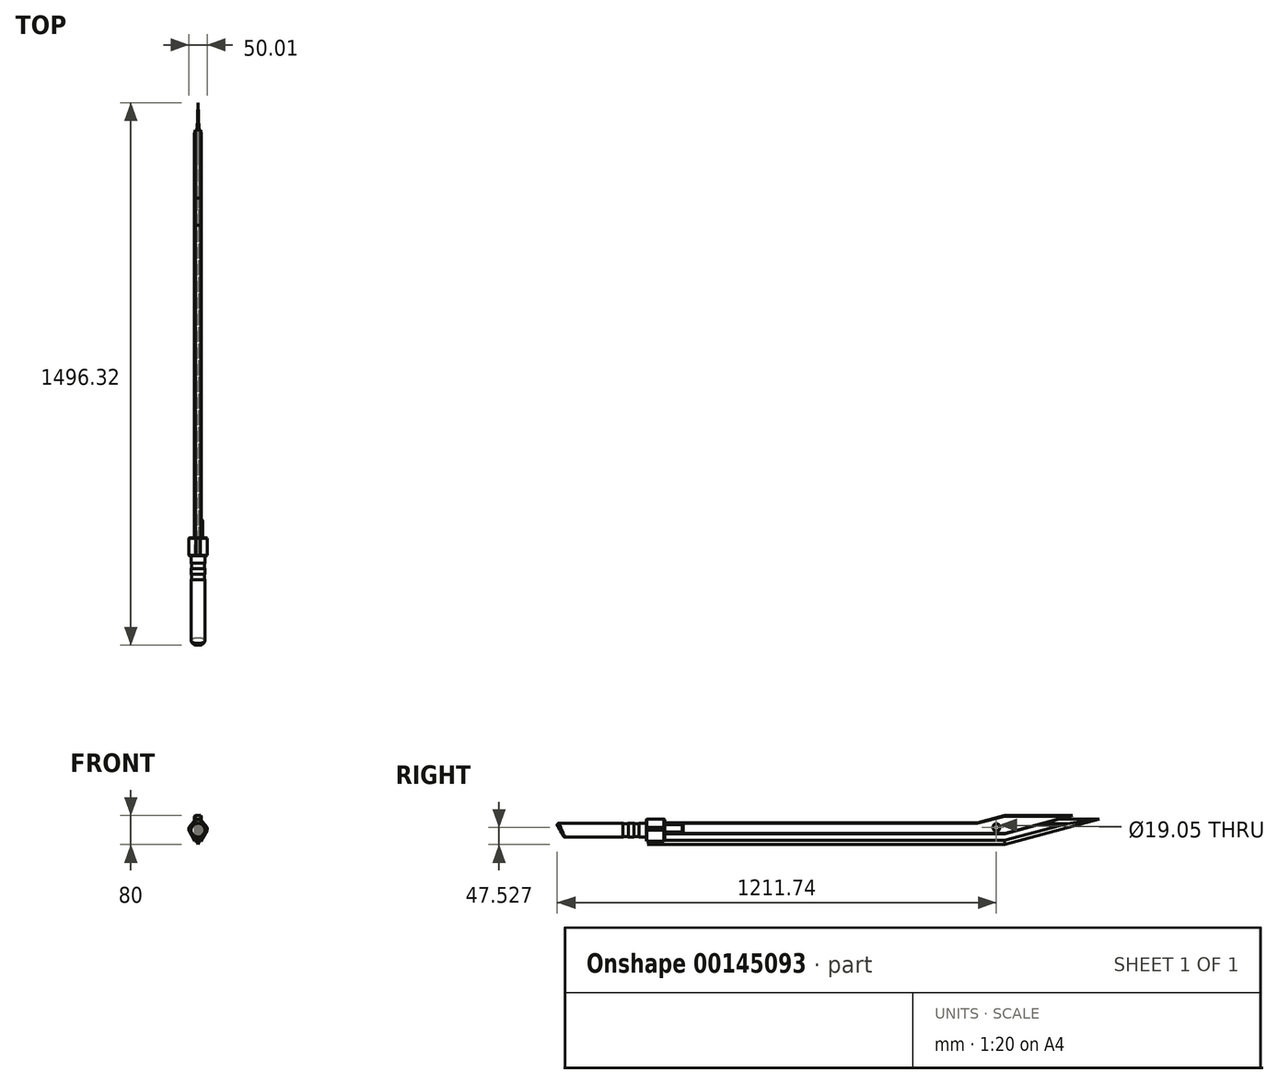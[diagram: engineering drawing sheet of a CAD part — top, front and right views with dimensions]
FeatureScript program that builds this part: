
annotation { "Feature Type Name" : "Feature", "Feature Type Description" : "" }
export const myFeature = defineFeature(function(context is Context, id is Id, definition is map)
    precondition{}
    {
        {
            var Q0;
            Q0=qCreatedBy(makeId("Right.planeOp"),FACE);
            var sketch = newSketch(context, id + "F0", { "sketchPlane" : qUnion([Q0])});
            skLineSegment(sketch, "E0", {"start": v(0, 0) * mm, "end": v(0, -19.92) * mm});
            skLineSegment(sketch, "E1", {"start": v(0, -19.92) * mm, "end": v(-47.25, -50) * mm});
            skLineSegment(sketch, "E2", {"start": v(-47.25, -50) * mm, "end": v(938.76, -50) * mm});
            skLineSegment(sketch, "E3", {"start": v(0, 0) * mm, "end": v(864.12, 0) * mm});
            skLineSegment(sketch, "E4", {"start": v(864.12, 0) * mm, "end": v(938.76, 20) * mm});
            skLineSegment(sketch, "E5", {"start": v(938.76, 20) * mm, "end": v(1200, 20) * mm});
            skLineSegment(sketch, "E6", {"start": v(1200, 20) * mm, "end": v(938.76, -50) * mm});
            skSolve(sketch);
        }
        {
            var Q0;
            Q0=makeQuery(id+"F0.imprint","IMPRINT",FACE,{"disambiguationData":[TD([[makeQuery(id+"F0.imprint","IMPRINT",EDGE,{"derivedFrom":sQuery(id+"F0.wireOp",EDGE,"E0")}),1.0]])]});
            extrude(context, id + "F1", {"entities" : qUnion([Q0]), "depth" : 6.35 * mm});
        }
        {
            var Q0;
            Q0=makeQuery(id+"F1.opExtrude","CAP_FACE",FACE,{"disambiguationData":[OSD([sQuery(id+"F0.wireOp",EDGE,"E0"),sQuery(id+"F0.wireOp",EDGE,"E1"),sQuery(id+"F0.wireOp",EDGE,"E2"),sQuery(id+"F0.wireOp",EDGE,"E3"),sQuery(id+"F0.wireOp",EDGE,"E4"),sQuery(id+"F0.wireOp",EDGE,"E5"),sQuery(id+"F0.wireOp",EDGE,"E6")])],"isStart":false});
            var sketch = newSketch(context, id + "F2", { "sketchPlane" : qUnion([Q0])});
            skLineSegment(sketch, "E7", {"start": v(0, -20) * mm, "end": v(938.76, -20) * mm});
            skPoint(sketch, "E8", {"position": v(1069.38, 20) * mm});
            skLineSegment(sketch, "E9", {"start": v(937.44, 30) * mm, "end": v(862.8, 10) * mm});
            skLineSegment(sketch, "E10", {"start": v(862.8, 10) * mm, "end": v(0, 10) * mm});
            skLineSegment(sketch, "E11", {"start": v(0, 10) * mm, "end": v(0, -20) * mm});
            skLineSegment(sketch, "E12", {"start": v(937.44, 30) * mm, "end": v(1125.36, 30) * mm});
            skLineSegment(sketch, "E13", {"start": v(1125.36, 30) * mm, "end": v(938.76, -20) * mm});
            skSolve(sketch);
        }
        {
            var Q0;
            Q0 = qSketchRegion(id + "F2", true);
            extrude(context, id + "F3", {"entities" : qUnion([Q0]), "operationType" : NewBodyOperationType.ADD, "depth" : 6.35 * mm});
        }
        {
            var Q0;
            Q0=makeQuery(id+"F3.opExtrude","CAP_FACE",FACE,{"disambiguationData":[OSD([sQuery(id+"F2.wireOp",EDGE,"E7"),sQuery(id+"F2.wireOp",EDGE,"E9"),sQuery(id+"F2.wireOp",EDGE,"E10"),sQuery(id+"F2.wireOp",EDGE,"E11"),sQuery(id+"F2.wireOp",EDGE,"E12"),sQuery(id+"F2.wireOp",EDGE,"E13")])],"isStart":true});
            var sketch = newSketch(context, id + "F4", { "sketchPlane" : qUnion([Q0])});
            skLineSegment(sketch, "E14", {"start": v(-1125.36, 30) * mm, "end": v(-1088.04, 20) * mm});
            skLineSegment(sketch, "E15", {"start": v(-1088.04, 20) * mm, "end": v(-938.76, 20) * mm});
            skLineSegment(sketch, "E16", {"start": v(-938.76, 20) * mm, "end": v(-864.12, 0) * mm});
            skLineSegment(sketch, "E17", {"start": v(-864.12, 0) * mm, "end": v(0, 0) * mm});
            skLineSegment(sketch, "E18", {"start": v(0, 0) * mm, "end": v(0, 10) * mm});
            skLineSegment(sketch, "E19", {"start": v(0, 10) * mm, "end": v(-862.8, 10) * mm});
            skLineSegment(sketch, "E20", {"start": v(-862.8, 10) * mm, "end": v(-937.44, 30) * mm});
            skLineSegment(sketch, "E21", {"start": v(-937.44, 30) * mm, "end": v(-1125.36, 30) * mm});
            skSolve(sketch);
        }
        {
            var Q0;
            Q0 = qSketchRegion(id + "F4", true);
            extrude(context, id + "F5", {"entities" : qUnion([Q0]), "operationType" : NewBodyOperationType.ADD, "depth" : 6.35 * mm});
        }
        {
            var Q0;
            Q0=makeQuery(id+"F5.boolean.opBoolean","MERGE",FACE,{"derivedFrom":[makeQuery(id+"F1.opExtrude","CAP_FACE",FACE,{"disambiguationData":[OSD([sQuery(id+"F0.wireOp",EDGE,"E0"),sQuery(id+"F0.wireOp",EDGE,"E1"),sQuery(id+"F0.wireOp",EDGE,"E2"),sQuery(id+"F0.wireOp",EDGE,"E3"),sQuery(id+"F0.wireOp",EDGE,"E4"),sQuery(id+"F0.wireOp",EDGE,"E5"),sQuery(id+"F0.wireOp",EDGE,"E6")])],"isStart":true}),makeQuery(id+"F5.opExtrude","CAP_FACE",FACE,{"disambiguationData":[OSD([sQuery(id+"F4.wireOp",EDGE,"E14"),sQuery(id+"F4.wireOp",EDGE,"E15"),sQuery(id+"F4.wireOp",EDGE,"E16"),sQuery(id+"F4.wireOp",EDGE,"E17"),sQuery(id+"F4.wireOp",EDGE,"E18"),sQuery(id+"F4.wireOp",EDGE,"E19"),sQuery(id+"F4.wireOp",EDGE,"E20"),sQuery(id+"F4.wireOp",EDGE,"E21")])],"isStart":false})]});
            var sketch = newSketch(context, id + "F6", { "sketchPlane" : qUnion([Q0])});
            skLineSegment(sketch, "E22", {"start": v(0, 10) * mm, "end": v(0, -20) * mm});
            skLineSegment(sketch, "E23", {"start": v(0, -20) * mm, "end": v(-938.76, -20) * mm});
            skLineSegment(sketch, "E24", {"start": v(-938.76, -20) * mm, "end": v(-1125.36, 30) * mm});
            skLineSegment(sketch, "E25", {"start": v(-1125.36, 30) * mm, "end": v(-937.44, 30) * mm});
            skLineSegment(sketch, "E26", {"start": v(-937.44, 30) * mm, "end": v(-862.8, 10) * mm});
            skLineSegment(sketch, "E27", {"start": v(-862.8, 10) * mm, "end": v(0, 10) * mm});
            skSolve(sketch);
        }
        {
            var Q0;
            Q0 = qSketchRegion(id + "F6", true);
            extrude(context, id + "F7", {"entities" : qUnion([Q0]), "operationType" : NewBodyOperationType.ADD, "depth" : 6.35 * mm});
        }
        {
            var Q0;
            Q0=makeQuery(id+"F7.boolean.opBoolean","MERGE",FACE,{"derivedFrom":[makeQuery(id+"F5.boolean.opBoolean","MERGE",FACE,{"derivedFrom":[makeQuery(id+"F3.boolean.opBoolean","MERGE",FACE,{"derivedFrom":[makeQuery(id+"F1.opExtrude","SWEPT_FACE",FACE,{"disambiguationData":[OSD([sQuery(id+"F0.wireOp",EDGE,"E0")])]}),makeQuery(id+"F3.opExtrude","SWEPT_FACE",FACE,{"disambiguationData":[OSD([sQuery(id+"F2.wireOp",EDGE,"E11")])]})]}),makeQuery(id+"F5.opExtrude","SWEPT_FACE",FACE,{"disambiguationData":[OSD([sQuery(id+"F4.wireOp",EDGE,"E18")])]})]}),makeQuery(id+"F7.opExtrude","SWEPT_FACE",FACE,{"disambiguationData":[OSD([sQuery(id+"F6.wireOp",EDGE,"E22")])]})]});
            var sketch = newSketch(context, id + "F8", { "sketchPlane" : qUnion([Q0])});
            skLineSegment(sketch, "E28.top", {"start": v(-21.82, -40) * mm, "end": v(28.18, -40) * mm});
            skLineSegment(sketch, "E28.left", {"start": v(-21.82, 20) * mm, "end": v(-21.82, -40) * mm});
            skLineSegment(sketch, "E28.right", {"start": v(28.18, 20) * mm, "end": v(28.18, -40) * mm});
            skLineSegment(sketch, "E29", {"start": v(-21.82, 20) * mm, "end": v(28.18, 20) * mm});
            skSolve(sketch);
        }
        {
            var Q0;
            Q0 = qSketchRegion(id + "F8", true);
            extrude(context, id + "F9", {"entities" : qUnion([Q0]), "operationType" : NewBodyOperationType.ADD, "depth" : 50 * mm});
        }
        {
            var Q0;
            Q0=makeQuery(id+"F9.opExtrude","CAP_FACE",FACE,{"disambiguationData":[OSD([sQuery(id+"F8.wireOp",EDGE,"E28.bottom"),sQuery(id+"F8.wireOp",EDGE,"E28.top"),sQuery(id+"F8.wireOp",EDGE,"E28.left"),sQuery(id+"F8.wireOp",EDGE,"E28.right")])],"isStart":false});
            var sketch = newSketch(context, id + "F10", { "sketchPlane" : qUnion([Q0])});
            skPoint(sketch, "E30.centerSnap0", {"position": v(3.18, -40) * mm});
            skCircle(sketch, "E31", {"center": v(3.17, -10) * mm, "radius": 19.05 * mm});
            skSolve(sketch);
        }
        {
            var Q0;
            Q0 = qSketchRegion(id + "F10", true);
            extrude(context, id + "F11", {"entities" : qUnion([Q0]), "operationType" : NewBodyOperationType.ADD, "depth" : 250 * mm});
        }
        {
            var Q0;
            Q0=makeQuery(id+"F1.opExtrude","CAP_EDGE",EDGE,{"disambiguationData":[OSD([sQuery(id+"F0.wireOp",EDGE,"E2")])],"isStart":false});
            var Q1;
            Q1=makeQuery(id+"F1.opExtrude","CAP_EDGE",EDGE,{"disambiguationData":[OSD([sQuery(id+"F0.wireOp",EDGE,"E2")])],"isStart":true});
            var Q2;
            Q2=makeQuery(id+"F1.opExtrude","CAP_EDGE",EDGE,{"disambiguationData":[OSD([sQuery(id+"F0.wireOp",EDGE,"E6")])],"isStart":false});
            var Q3;
            {var subQ1=sQuery(id+"F0.wireOp",EDGE,"E5");var subQ2=sQuery(id+"F0.wireOp",EDGE,"E6");Q3=makeQuery(id+"F3.boolean.opBoolean","SPLIT",EDGE,{"disambiguationData":[TD([makeQuery(id+"F1.opExtrude","SWEPT_FACE",FACE,{"disambiguationData":[OSD([subQ2])]})])],"derivedFrom":makeQuery(id+"F1.opExtrude","CAP_EDGE",EDGE,{"disambiguationData":[OSD([subQ1])],"isStart":false})});}
            var Q4;
            Q4=makeQuery(id+"F1.opExtrude","CAP_EDGE",EDGE,{"disambiguationData":[OSD([sQuery(id+"F0.wireOp",EDGE,"E5")])],"isStart":true});
            var Q5;
            Q5=makeQuery(id+"F1.opExtrude","CAP_EDGE",EDGE,{"disambiguationData":[OSD([sQuery(id+"F0.wireOp",EDGE,"E6")])],"isStart":true});
            chamfer(context, id + "F12", {"entities" : qUnion([Q0, Q1, Q2, Q3, Q4, Q5]), "chamferType" : ChamferType.OFFSET_ANGLE, "width" : 3.17 * mm, "oppositeDirection" : true, "angle" : 75 * degree, "tangentPropagation" : true});
        }
        {
            var Q0;
            Q0=qCreatedBy(makeId("Right.planeOp"),FACE);
            cPlane(context, id + "F13", {"entities" : qUnion([Q0]), "cplaneType" : CPlaneType.OFFSET, "offset" : 3.17 * mm, "width" : 150 * mm, "height" : 150 * mm});
        }
        {
            var Q0;
            Q0=qCreatedBy(id+"F13.planeOp",FACE);
            var sketch = newSketch(context, id + "F14", { "sketchPlane" : qUnion([Q0])});
            skLineSegment(sketch, "E32.bottom", {"start": v(-115, 9.05) * mm, "end": v(-100, 9.05) * mm});
            skLineSegment(sketch, "E32.top", {"start": v(-115, 7.8) * mm, "end": v(-100, 7.8) * mm});
            skLineSegment(sketch, "E32.left", {"start": v(-115, 9.05) * mm, "end": v(-115, 7.8) * mm});
            skLineSegment(sketch, "E32.right", {"start": v(-100, 9.05) * mm, "end": v(-100, 7.8) * mm});
            skLineSegment(sketch, "E33.bottom", {"start": v(-85, 9.05) * mm, "end": v(-70, 9.05) * mm});
            skLineSegment(sketch, "E33.top", {"start": v(-85, 7.8) * mm, "end": v(-70, 7.8) * mm});
            skLineSegment(sketch, "E33.left", {"start": v(-85, 9.05) * mm, "end": v(-85, 7.8) * mm});
            skLineSegment(sketch, "E33.right", {"start": v(-70, 9.05) * mm, "end": v(-70, 7.8) * mm});
            skLineSegment(sketch, "E34", {"start": v(-220.02, -10) * mm, "end": v(-50, -10) * mm});
            skSolve(sketch);
        }
        {
            var Q0;
            Q0 = qSketchRegion(id + "F14", true);
            var Q1;
            Q1=sQuery(id+"F14.wireOp",EDGE,"E34");
            revolve(context, id + "F15", {"operationType" : NewBodyOperationType.REMOVE, "entities" : qUnion([Q0]), "axis" : qUnion([Q1]), "revolveType" : RevolveType.FULL, "oppositeDirection" : true});
        }
        {
            var Q0;
            Q0=makeQuery(id+"F15.boolean.opBoolean","COPY",FACE,{"derivedFrom":makeQuery(id+"F15.opRevolve","SWEPT_FACE",FACE,{"disambiguationData":[OSD([sQuery(id+"F14.wireOp",EDGE,"E32.top")])]})});
            var Q1;
            Q1=makeQuery(id+"F15.boolean.opBoolean","COPY",FACE,{"derivedFrom":makeQuery(id+"F15.opRevolve","SWEPT_FACE",FACE,{"disambiguationData":[OSD([sQuery(id+"F14.wireOp",EDGE,"E33.top")])]})});
            fillet(context, id + "F16", {"entities" : qUnion([Q0, Q1]), "radius" : 5 * mm, "tangentPropagation" : true, "allowEdgeOverflow" : false});
        }
        {
            var Q0;
            Q0=makeQuery(id+"F9.opExtrude","SWEPT_EDGE",EDGE,{"disambiguationData":[OSD([sQuery(id+"F8.wireOp",EDGE,"E28.right"),sQuery(id+"F8.wireOp",EDGE,"E29")])]});
            var Q1;
            Q1=makeQuery(id+"F9.opExtrude","SWEPT_EDGE",EDGE,{"disambiguationData":[OSD([sQuery(id+"F8.wireOp",EDGE,"E28.left"),sQuery(id+"F8.wireOp",EDGE,"E29")])]});
            chamfer(context, id + "F17", {"entities" : qUnion([Q0, Q1]), "chamferType" : ChamferType.OFFSET_ANGLE, "width" : 18.8 * mm, "oppositeDirection" : false, "angle" : 50 * degree, "tangentPropagation" : true});
        }
        {
            var Q0;
            Q0=makeQuery(id+"F9.opExtrude","SWEPT_EDGE",EDGE,{"disambiguationData":[OSD([sQuery(id+"F8.wireOp",EDGE,"E28.top"),sQuery(id+"F8.wireOp",EDGE,"E28.right")])]});
            var Q1;
            Q1=makeQuery(id+"F9.opExtrude","SWEPT_EDGE",EDGE,{"disambiguationData":[OSD([sQuery(id+"F8.wireOp",EDGE,"E28.top"),sQuery(id+"F8.wireOp",EDGE,"E28.left")])]});
            chamfer(context, id + "F18", {"entities" : qUnion([Q0, Q1]), "chamferType" : ChamferType.OFFSET_ANGLE, "width" : 30 * mm, "oppositeDirection" : false, "angle" : 29 * degree, "tangentPropagation" : true});
        }
        {
            var Q0;
            Q0=qCreatedBy(makeId("Right.planeOp"),FACE);
            var sketch = newSketch(context, id + "F19", { "sketchPlane" : qUnion([Q0])});
            skLineSegment(sketch, "E35", {"start": v(-300, 9.08) * mm, "end": v(-277.97, -29.08) * mm});
            skLineSegment(sketch, "E36", {"start": v(-300, -29.08) * mm, "end": v(-300, 9.08) * mm});
            skLineSegment(sketch, "E37", {"start": v(-300, -29.08) * mm, "end": v(-277.97, -29.08) * mm});
            skSolve(sketch);
        }
        {
            var Q0;
            Q0=makeQuery(id+"F19.imprint","IMPRINT",FACE,{"disambiguationData":[TD([[makeQuery(id+"F19.imprint","IMPRINT",EDGE,{"derivedFrom":sQuery(id+"F19.wireOp",EDGE,"E35")}),-1.0]])]});
            extrude(context, id + "F20", {"entities" : qUnion([Q0]), "operationType" : NewBodyOperationType.REMOVE, "depth" : 25 * mm, "hasSecondDirection" : true, "secondDirectionOppositeDirection" : true, "secondDirectionDepth" : 25 * mm});
        }
        {
            var Q0;
            {var subQ0=sQuery(id+"F10.wireOp",EDGE,"E31");Q0=makeQuery(id+"F20.boolean.opBoolean","INTERSECT",EDGE,{"derivedFrom":[makeQuery(id+"F15.boolean.opBoolean","SPLIT",FACE,{"disambiguationData":[TD([makeQuery(id+"F11.opExtrude","CAP_FACE",FACE,{"disambiguationData":[OSD([subQ0])],"isStart":false})])],"derivedFrom":makeQuery(id+"F11.opExtrude","SWEPT_FACE",FACE,{"disambiguationData":[OSD([subQ0])]})}),makeQuery(id+"F20.opExtrude","SWEPT_FACE",FACE,{"disambiguationData":[OSD([sQuery(id+"F19.wireOp",EDGE,"E35")])]})]});}
            fillet(context, id + "F21", {"entities" : qUnion([Q0]), "radius" : 5 * mm, "tangentPropagation" : true, "allowEdgeOverflow" : false});
        }
        {
            var Q0;
            Q0=makeQuery(id+"F3.opExtrude","CAP_FACE",FACE,{"disambiguationData":[OSD([sQuery(id+"F2.wireOp",EDGE,"E7"),sQuery(id+"F2.wireOp",EDGE,"E9"),sQuery(id+"F2.wireOp",EDGE,"E10"),sQuery(id+"F2.wireOp",EDGE,"E11"),sQuery(id+"F2.wireOp",EDGE,"E12"),sQuery(id+"F2.wireOp",EDGE,"E13")])],"isStart":false});
            var sketch = newSketch(context, id + "F22", { "sketchPlane" : qUnion([Q0])});
            skCircle(sketch, "E38", {"center": v(915.42, -2.47) * mm, "radius": 9.53 * mm});
            skSolve(sketch);
        }
        {
            var Q0;
            Q0 = qSketchRegion(id + "F22", true);
            extrude(context, id + "F23", {"entities" : qUnion([Q0]), "operationType" : NewBodyOperationType.REMOVE, "oppositeDirection" : true, "depth" : 25 * mm});
        }
        {
            var Q0;
            Q0=makeQuery(id+"F23.boolean.opBoolean","INTERSECT",EDGE,{"derivedFrom":[makeQuery(id+"F7.opExtrude","CAP_FACE",FACE,{"disambiguationData":[OSD([sQuery(id+"F6.wireOp",EDGE,"E22"),sQuery(id+"F6.wireOp",EDGE,"E23"),sQuery(id+"F6.wireOp",EDGE,"E24"),sQuery(id+"F6.wireOp",EDGE,"E25"),sQuery(id+"F6.wireOp",EDGE,"E26"),sQuery(id+"F6.wireOp",EDGE,"E27")])],"isStart":false}),makeQuery(id+"F23.opExtrude","SWEPT_FACE",FACE,{"disambiguationData":[OSD([sQuery(id+"F22.wireOp",EDGE,"E38")])]})]});
            var Q1;
            Q1=makeQuery(id+"F23.boolean.opBoolean","COPY",EDGE,{"derivedFrom":makeQuery(id+"F23.opExtrude","CAP_EDGE",EDGE,{"disambiguationData":[OSD([sQuery(id+"F22.wireOp",EDGE,"E38")])],"isStart":true})});
            chamfer(context, id + "F24", {"entities" : qUnion([Q0, Q1]), "width" : 2.5 * mm, "tangentPropagation" : true});
        }
        {
            var Q0;
            Q0=makeQuery(id+"F7.opExtrude","CAP_EDGE",EDGE,{"disambiguationData":[OSD([sQuery(id+"F6.wireOp",EDGE,"E27")])],"isStart":false});
            var Q1;
            Q1=makeQuery(id+"F3.opExtrude","CAP_EDGE",EDGE,{"disambiguationData":[OSD([sQuery(id+"F2.wireOp",EDGE,"E10")])],"isStart":false});
            var Q2;
            Q2=makeQuery(id+"F7.opExtrude","CAP_EDGE",EDGE,{"disambiguationData":[OSD([sQuery(id+"F6.wireOp",EDGE,"E25")])],"isStart":false});
            var Q3;
            Q3=makeQuery(id+"F3.opExtrude","CAP_EDGE",EDGE,{"disambiguationData":[OSD([sQuery(id+"F2.wireOp",EDGE,"E12")])],"isStart":false});
            var Q4;
            Q4=makeQuery(id+"F3.opExtrude","CAP_EDGE",EDGE,{"disambiguationData":[OSD([sQuery(id+"F2.wireOp",EDGE,"E9")])],"isStart":false});
            var Q5;
            Q5=makeQuery(id+"F7.opExtrude","CAP_EDGE",EDGE,{"disambiguationData":[OSD([sQuery(id+"F6.wireOp",EDGE,"E26")])],"isStart":false});
            var Q6;
            Q6=makeQuery(id+"F3.opExtrude","CAP_EDGE",EDGE,{"disambiguationData":[OSD([sQuery(id+"F2.wireOp",EDGE,"E13")])],"isStart":false});
            var Q7;
            Q7=makeQuery(id+"F7.opExtrude","CAP_EDGE",EDGE,{"disambiguationData":[OSD([sQuery(id+"F6.wireOp",EDGE,"E23")])],"isStart":false});
            var Q8;
            {var subQ0=sQuery(id+"F8.wireOp",EDGE,"E28.left");var subQ1=sQuery(id+"F8.wireOp",EDGE,"E28.top");Q8=makeQuery(id+"F18.opChamfer","BLEND_EDGE",EDGE,{"blendedFrom":[makeQuery(id+"F9.opExtrude","SWEPT_EDGE",EDGE,{"disambiguationData":[OSD([subQ1,subQ0])]}),makeQuery(id+"F9.opExtrude","CAP_FACE",FACE,{"disambiguationData":[OSD([subQ1,subQ0,sQuery(id+"F8.wireOp",EDGE,"E28.right"),sQuery(id+"F8.wireOp",EDGE,"E29")])],"isStart":true})],"blendedInto":[makeQuery(id+"F9.opExtrude","CAP_FACE",FACE,{"disambiguationData":[OSD([subQ1,subQ0,sQuery(id+"F8.wireOp",EDGE,"E28.right"),sQuery(id+"F8.wireOp",EDGE,"E29")])],"isStart":true})]});}
            var Q9;
            {var subQ0=sQuery(id+"F8.wireOp",EDGE,"E29");var subQ1=sQuery(id+"F8.wireOp",EDGE,"E28.left");Q9=makeQuery(id+"F17.opChamfer","BLEND_EDGE",EDGE,{"blendedFrom":[makeQuery(id+"F9.opExtrude","SWEPT_EDGE",EDGE,{"disambiguationData":[OSD([subQ1,subQ0])]}),makeQuery(id+"F9.opExtrude","CAP_FACE",FACE,{"disambiguationData":[OSD([sQuery(id+"F8.wireOp",EDGE,"E28.top"),subQ1,sQuery(id+"F8.wireOp",EDGE,"E28.right"),subQ0])],"isStart":true})],"blendedInto":[makeQuery(id+"F9.opExtrude","CAP_FACE",FACE,{"disambiguationData":[OSD([sQuery(id+"F8.wireOp",EDGE,"E28.top"),subQ1,sQuery(id+"F8.wireOp",EDGE,"E28.right"),subQ0])],"isStart":true})]});}
            var Q10;
            Q10=makeQuery(id+"F9.opExtrude","CAP_EDGE",EDGE,{"disambiguationData":[OSD([sQuery(id+"F8.wireOp",EDGE,"E28.left")])],"isStart":true});
            var Q11;
            {var subQ0=sQuery(id+"F8.wireOp",EDGE,"E28.left");var subQ1=sQuery(id+"F8.wireOp",EDGE,"E28.top");Q11=makeQuery(id+"F9.boolean.opBoolean","SPLIT",EDGE,{"disambiguationData":[TD([makeQuery(id+"F9.opExtrude","SWEPT_FACE",FACE,{"disambiguationData":[OSD([subQ0])]})])],"derivedFrom":makeQuery(id+"F9.opExtrude","CAP_EDGE",EDGE,{"disambiguationData":[OSD([subQ1])],"isStart":true})});}
            var Q12;
            {var subQ0=sQuery(id+"F8.wireOp",EDGE,"E28.top");var subQ1=sQuery(id+"F8.wireOp",EDGE,"E28.right");Q12=makeQuery(id+"F9.boolean.opBoolean","SPLIT",EDGE,{"disambiguationData":[TD([makeQuery(id+"F9.opExtrude","SWEPT_FACE",FACE,{"disambiguationData":[OSD([subQ1])]})])],"derivedFrom":makeQuery(id+"F9.opExtrude","CAP_EDGE",EDGE,{"disambiguationData":[OSD([subQ0])],"isStart":true})});}
            var Q13;
            {var subQ0=sQuery(id+"F8.wireOp",EDGE,"E28.right");var subQ1=sQuery(id+"F8.wireOp",EDGE,"E28.top");Q13=makeQuery(id+"F18.opChamfer","BLEND_EDGE",EDGE,{"blendedFrom":[makeQuery(id+"F9.opExtrude","SWEPT_EDGE",EDGE,{"disambiguationData":[OSD([subQ1,subQ0])]}),makeQuery(id+"F9.opExtrude","CAP_FACE",FACE,{"disambiguationData":[OSD([subQ1,sQuery(id+"F8.wireOp",EDGE,"E28.left"),subQ0,sQuery(id+"F8.wireOp",EDGE,"E29")])],"isStart":true})],"blendedInto":[makeQuery(id+"F9.opExtrude","CAP_FACE",FACE,{"disambiguationData":[OSD([subQ1,sQuery(id+"F8.wireOp",EDGE,"E28.left"),subQ0,sQuery(id+"F8.wireOp",EDGE,"E29")])],"isStart":true})]});}
            var Q14;
            Q14=makeQuery(id+"F9.opExtrude","CAP_EDGE",EDGE,{"disambiguationData":[OSD([sQuery(id+"F8.wireOp",EDGE,"E28.right")])],"isStart":true});
            var Q15;
            {var subQ0=sQuery(id+"F8.wireOp",EDGE,"E29");var subQ1=sQuery(id+"F8.wireOp",EDGE,"E28.right");Q15=makeQuery(id+"F17.opChamfer","BLEND_EDGE",EDGE,{"blendedFrom":[makeQuery(id+"F9.opExtrude","SWEPT_EDGE",EDGE,{"disambiguationData":[OSD([subQ1,subQ0])]}),makeQuery(id+"F9.opExtrude","CAP_FACE",FACE,{"disambiguationData":[OSD([sQuery(id+"F8.wireOp",EDGE,"E28.top"),sQuery(id+"F8.wireOp",EDGE,"E28.left"),subQ1,subQ0])],"isStart":true})],"blendedInto":[makeQuery(id+"F9.opExtrude","CAP_FACE",FACE,{"disambiguationData":[OSD([sQuery(id+"F8.wireOp",EDGE,"E28.top"),sQuery(id+"F8.wireOp",EDGE,"E28.left"),subQ1,subQ0])],"isStart":true})]});}
            var Q16;
            Q16=makeQuery(id+"F9.opExtrude","CAP_EDGE",EDGE,{"disambiguationData":[OSD([sQuery(id+"F8.wireOp",EDGE,"E29")])],"isStart":true});
            var Q17;
            {var subQ0=sQuery(id+"F8.wireOp",EDGE,"E29");var subQ1=sQuery(id+"F8.wireOp",EDGE,"E28.right");Q17=makeQuery(id+"F17.opChamfer","BLEND_EDGE",EDGE,{"blendedFrom":[makeQuery(id+"F9.opExtrude","SWEPT_EDGE",EDGE,{"disambiguationData":[OSD([subQ1,subQ0])]}),makeQuery(id+"F9.opExtrude","CAP_FACE",FACE,{"disambiguationData":[OSD([sQuery(id+"F8.wireOp",EDGE,"E28.top"),sQuery(id+"F8.wireOp",EDGE,"E28.left"),subQ1,subQ0])],"isStart":false})],"blendedInto":[makeQuery(id+"F9.opExtrude","CAP_FACE",FACE,{"disambiguationData":[OSD([sQuery(id+"F8.wireOp",EDGE,"E28.top"),sQuery(id+"F8.wireOp",EDGE,"E28.left"),subQ1,subQ0])],"isStart":false})]});}
            var Q18;
            Q18=makeQuery(id+"F9.opExtrude","CAP_EDGE",EDGE,{"disambiguationData":[OSD([sQuery(id+"F8.wireOp",EDGE,"E29")])],"isStart":false});
            var Q19;
            {var subQ0=sQuery(id+"F8.wireOp",EDGE,"E29");var subQ1=sQuery(id+"F8.wireOp",EDGE,"E28.left");Q19=makeQuery(id+"F17.opChamfer","BLEND_EDGE",EDGE,{"blendedFrom":[makeQuery(id+"F9.opExtrude","SWEPT_EDGE",EDGE,{"disambiguationData":[OSD([subQ1,subQ0])]}),makeQuery(id+"F9.opExtrude","CAP_FACE",FACE,{"disambiguationData":[OSD([sQuery(id+"F8.wireOp",EDGE,"E28.top"),subQ1,sQuery(id+"F8.wireOp",EDGE,"E28.right"),subQ0])],"isStart":false})],"blendedInto":[makeQuery(id+"F9.opExtrude","CAP_FACE",FACE,{"disambiguationData":[OSD([sQuery(id+"F8.wireOp",EDGE,"E28.top"),subQ1,sQuery(id+"F8.wireOp",EDGE,"E28.right"),subQ0])],"isStart":false})]});}
            var Q20;
            Q20=makeQuery(id+"F9.opExtrude","CAP_EDGE",EDGE,{"disambiguationData":[OSD([sQuery(id+"F8.wireOp",EDGE,"E28.right")])],"isStart":false});
            var Q21;
            {var subQ0=sQuery(id+"F8.wireOp",EDGE,"E28.right");var subQ1=sQuery(id+"F8.wireOp",EDGE,"E28.top");Q21=makeQuery(id+"F18.opChamfer","BLEND_EDGE",EDGE,{"blendedFrom":[makeQuery(id+"F9.opExtrude","SWEPT_EDGE",EDGE,{"disambiguationData":[OSD([subQ1,subQ0])]}),makeQuery(id+"F9.opExtrude","CAP_FACE",FACE,{"disambiguationData":[OSD([subQ1,sQuery(id+"F8.wireOp",EDGE,"E28.left"),subQ0,sQuery(id+"F8.wireOp",EDGE,"E29")])],"isStart":false})],"blendedInto":[makeQuery(id+"F9.opExtrude","CAP_FACE",FACE,{"disambiguationData":[OSD([subQ1,sQuery(id+"F8.wireOp",EDGE,"E28.left"),subQ0,sQuery(id+"F8.wireOp",EDGE,"E29")])],"isStart":false})]});}
            var Q22;
            {var subQ0=sQuery(id+"F8.wireOp",EDGE,"E28.left");var subQ1=sQuery(id+"F8.wireOp",EDGE,"E28.top");Q22=makeQuery(id+"F18.opChamfer","BLEND_EDGE",EDGE,{"blendedFrom":[makeQuery(id+"F9.opExtrude","SWEPT_EDGE",EDGE,{"disambiguationData":[OSD([subQ1,subQ0])]}),makeQuery(id+"F9.opExtrude","CAP_FACE",FACE,{"disambiguationData":[OSD([subQ1,subQ0,sQuery(id+"F8.wireOp",EDGE,"E28.right"),sQuery(id+"F8.wireOp",EDGE,"E29")])],"isStart":false})],"blendedInto":[makeQuery(id+"F9.opExtrude","CAP_FACE",FACE,{"disambiguationData":[OSD([subQ1,subQ0,sQuery(id+"F8.wireOp",EDGE,"E28.right"),sQuery(id+"F8.wireOp",EDGE,"E29")])],"isStart":false})]});}
            var Q23;
            Q23=makeQuery(id+"F9.opExtrude","CAP_EDGE",EDGE,{"disambiguationData":[OSD([sQuery(id+"F8.wireOp",EDGE,"E28.top")])],"isStart":false});
            var Q24;
            Q24=makeQuery(id+"F9.opExtrude","CAP_EDGE",EDGE,{"disambiguationData":[OSD([sQuery(id+"F8.wireOp",EDGE,"E28.left")])],"isStart":false});
            var Q25;
            Q25=makeQuery(id+"F7.opExtrude","CAP_EDGE",EDGE,{"disambiguationData":[OSD([sQuery(id+"F6.wireOp",EDGE,"E24")])],"isStart":false});
            var Q26;
            Q26=makeQuery(id+"F3.opExtrude","CAP_EDGE",EDGE,{"disambiguationData":[OSD([sQuery(id+"F2.wireOp",EDGE,"E7")])],"isStart":false});
            chamfer(context, id + "F25", {"entities" : qUnion([Q0, Q1, Q2, Q3, Q4, Q5, Q6, Q7, Q8, Q9, Q10, Q11, Q12, Q13, Q14, Q15, Q16, Q17, Q18, Q19, Q20, Q21, Q22, Q23, Q24, Q25, Q26]), "width" : 1.5 * mm, "tangentPropagation" : true});
        }
        {
            var Q0;
            Q0=makeQuery(id+"F3.opExtrude","CAP_FACE",FACE,{"disambiguationData":[OSD([sQuery(id+"F2.wireOp",EDGE,"E7"),sQuery(id+"F2.wireOp",EDGE,"E9"),sQuery(id+"F2.wireOp",EDGE,"E10"),sQuery(id+"F2.wireOp",EDGE,"E11"),sQuery(id+"F2.wireOp",EDGE,"E12"),sQuery(id+"F2.wireOp",EDGE,"E13")])],"isStart":false});
            var sketch = newSketch(context, id + "F26", { "sketchPlane" : qUnion([Q0])});
            skLineSegment(sketch, "E39.bottom", {"start": v(0, 7.57) * mm, "end": v(50.8, 7.57) * mm});
            skLineSegment(sketch, "E39.top", {"start": v(0, -17.83) * mm, "end": v(50.8, -17.83) * mm});
            skLineSegment(sketch, "E39.left", {"start": v(0, 7.57) * mm, "end": v(0, -17.83) * mm});
            skLineSegment(sketch, "E39.right", {"start": v(50.8, 7.57) * mm, "end": v(50.8, -17.83) * mm});
            skSolve(sketch);
        }
        {
            var Q0;
            Q0 = qSketchRegion(id + "F26", true);
            extrude(context, id + "F27", {"entities" : qUnion([Q0]), "operationType" : NewBodyOperationType.ADD, "depth" : 3.17 * mm});
        }
        {
            var Q0;
            Q0=makeQuery(id+"F27.opExtrude","CAP_EDGE",EDGE,{"disambiguationData":[OSD([sQuery(id+"F26.wireOp",EDGE,"E39.bottom")])],"isStart":false});
            var Q1;
            Q1=makeQuery(id+"F27.opExtrude","CAP_EDGE",EDGE,{"disambiguationData":[OSD([sQuery(id+"F26.wireOp",EDGE,"E39.right")])],"isStart":false});
            var Q2;
            Q2=makeQuery(id+"F27.opExtrude","CAP_EDGE",EDGE,{"disambiguationData":[OSD([sQuery(id+"F26.wireOp",EDGE,"E39.top")])],"isStart":false});
            chamfer(context, id + "F28", {"entities" : qUnion([Q0, Q1, Q2]), "width" : 2.5 * mm, "tangentPropagation" : true});
        }
    });
